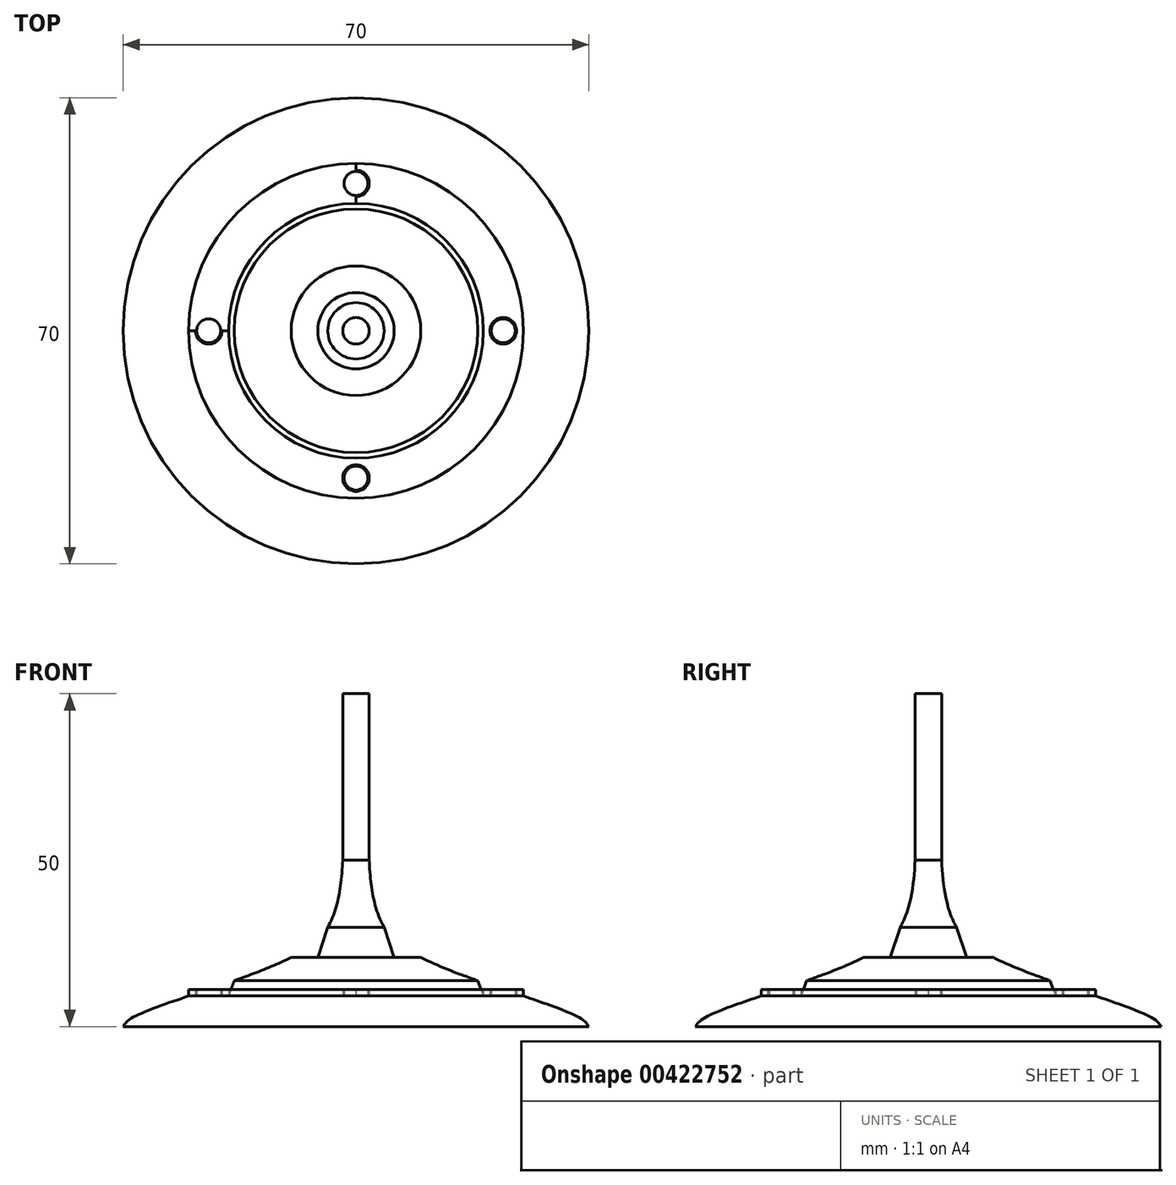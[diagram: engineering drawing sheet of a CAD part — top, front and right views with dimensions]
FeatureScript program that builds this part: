
annotation { "Feature Type Name" : "Feature", "Feature Type Description" : "" }
export const myFeature = defineFeature(function(context is Context, id is Id, definition is map)
    precondition{}
    {
        {
            var Q0;
            Q0=qCreatedBy(makeId("Front.planeOp"),FACE);
            var sketch = newSketch(context, id + "F0", { "sketchPlane" : qUnion([Q0])});
            skLineSegment(sketch, "E0", {"start": v(0, 0) * mm, "end": v(-35, 0) * mm});
            skLineSegment(sketch, "E1", {"start": v(0, 0) * mm, "end": v(0, 50) * mm});
            skLineSegment(sketch, "E2.bottom", {"start": v(0, 50) * mm, "end": v(-2, 50) * mm});
            skLineSegment(sketch, "E2.top", {"start": v(0, 25) * mm, "end": v(-2, 25) * mm});
            skLineSegment(sketch, "E2.left", {"start": v(0, 50) * mm, "end": v(0, 25) * mm});
            skLineSegment(sketch, "E2.right", {"start": v(-2, 50) * mm, "end": v(-2, 25) * mm});
            skLineSegment(sketch, "E3", {"start": v(0, 10.57) * mm, "end": v(-1, 10.57) * mm});
            skPoint(sketch, "E3.endSnap0", {"position": v(-1, 25) * mm});
            skFitSpline(sketch, "E4", {"points": [v(-35, 0) * mm, v(-33.81, 1.19) * mm, v(-25.13, 4.58) * mm, v(-18.3, 6.9) * mm, v(-9.74, 10.37) * mm, v(-4.24, 14.92) * mm, v(-2, 25) * mm], "startDerivative": vector(9.24, 13.84) * mm, "endDerivative": vector(1.73, 56.25) * mm});
            skLineSegment(sketch, "E5", {"start": v(-25.13, 4.58) * mm, "end": v(-19.13, 4.58) * mm});
            skLineSegment(sketch, "E6", {"start": v(-19.13, 4.58) * mm, "end": v(-18.3, 6.9) * mm});
            skLineSegment(sketch, "E7", {"start": v(-9.74, 10.37) * mm, "end": v(-5.74, 10.37) * mm});
            skLineSegment(sketch, "E8", {"start": v(-5.74, 10.37) * mm, "end": v(-4.24, 14.92) * mm});
            skSolve(sketch);
        }
        {
            var Q0;
            Q0=makeQuery(id+"F0.imprint","IMPRINT",FACE,{"disambiguationData":[TD([[makeQuery(id+"F0.imprint","IMPRINT",EDGE,{"derivedFrom":sQuery(id+"F0.wireOp",EDGE,"E2.bottom")}),1.0]])]});
            var Q1;
            {var subQ3=sQuery(id+"F0.wireOp",EDGE,"E0");Q1=makeQuery(id+"F0.imprint","IMPRINT",FACE,{"disambiguationData":[TD([[makeQuery(id+"F0.imprint","IMPRINT",EDGE,{"derivedFrom":subQ3}),-1.0]])]});}
            var Q2;
            Q2=sQuery(id+"F0.wireOp",EDGE,"E1");
            revolve(context, id + "F1", {"entities" : qUnion([Q0, Q1]), "axis" : qUnion([Q2]), "revolveType" : RevolveType.FULL});
        }
        {
            var Q0;
            Q0=makeQuery(id+"F1.opRevolve","SWEPT_FACE",FACE,{"disambiguationData":[OSD([sQuery(id+"F0.wireOp",EDGE,"E5")])]});
            var sketch = newSketch(context, id + "F2", { "sketchPlane" : qUnion([Q0])});
            skLineSegment(sketch, "E9", {"start": v(0, -19.13) * mm, "end": v(0, -25.13) * mm});
            skCircle(sketch, "E10", {"center": v(0, -22.13) * mm, "radius": 2 * mm});
            skCircle(sketch, "E11.0", {"center": v(0, -22.13) * mm, "radius": 1.8 * mm});
            skLineSegment(sketch, "E12", {"start": v(19.13, 0) * mm, "end": v(25.13, 0) * mm});
            skCircle(sketch, "E13", {"center": v(22.13, 0) * mm, "radius": 2 * mm});
            skCircle(sketch, "E14.0", {"center": v(22.13, 0) * mm, "radius": 1.8 * mm});
            skLineSegment(sketch, "E15", {"start": v(0, 19.13) * mm, "end": v(0, 25.13) * mm});
            skCircle(sketch, "E16", {"center": v(0, 22.13) * mm, "radius": 2 * mm});
            skCircle(sketch, "E17.0", {"center": v(0, 22.13) * mm, "radius": 1.8 * mm});
            skLineSegment(sketch, "E18", {"start": v(-19.13, 0) * mm, "end": v(-25.13, 0) * mm});
            skCircle(sketch, "E19", {"center": v(-22.13, 0) * mm, "radius": 2 * mm});
            skCircle(sketch, "E20.0", {"center": v(-22.13, 0) * mm, "radius": 1.8 * mm});
            skSolve(sketch);
        }
        {
            var Q0;
            {var subQ6=sQuery(id+"F2.wireOp",EDGE,"E10");var subQ7=sQuery(id+"F2.wireOp",EDGE,"E9");var subQ8=makeQuery(id+"F2.imprint","INTERSECT",VERTEX,{"disambiguationData":[OD(0.0)],"derivedFrom":[subQ7,subQ6]});Q0=makeQuery(id+"F2.imprint","IMPRINT",FACE,{"disambiguationData":[TD([[makeQuery(id+"F2.imprint","IMPRINT",EDGE,{"disambiguationData":[TD([[subQ8,-1.0]])],"derivedFrom":subQ6}),-1.0]])]});}
            var Q1;
            {var subQ0=sQuery(id+"F2.wireOp",EDGE,"E10");var subQ1=sQuery(id+"F2.wireOp",EDGE,"E9");var subQ2=makeQuery(id+"F2.imprint","INTERSECT",VERTEX,{"disambiguationData":[OD(0.0)],"derivedFrom":[subQ1,subQ0]});Q1=makeQuery(id+"F2.imprint","IMPRINT",FACE,{"disambiguationData":[TD([[makeQuery(id+"F2.imprint","IMPRINT",EDGE,{"disambiguationData":[TD([[subQ2,1.0]])],"derivedFrom":subQ0}),-1.0]])]});}
            var Q2;
            {var subQ6=sQuery(id+"F2.wireOp",EDGE,"E12");var subQ9=sQuery(id+"F2.wireOp",EDGE,"E13");var subQ12=makeQuery(id+"F2.imprint","INTERSECT",VERTEX,{"disambiguationData":[OD(0.0)],"derivedFrom":[subQ6,subQ9]});Q2=makeQuery(id+"F2.imprint","IMPRINT",FACE,{"disambiguationData":[TD([[makeQuery(id+"F2.imprint","IMPRINT",EDGE,{"disambiguationData":[TD([[subQ12,1.0]])],"derivedFrom":subQ9}),-1.0]])]});}
            var Q3;
            {var subQ6=sQuery(id+"F2.wireOp",EDGE,"E15");var subQ9=sQuery(id+"F2.wireOp",EDGE,"E16");var subQ11=makeQuery(id+"F2.imprint","INTERSECT",VERTEX,{"disambiguationData":[OD(0.0)],"derivedFrom":[subQ6,subQ9]});Q3=makeQuery(id+"F2.imprint","IMPRINT",FACE,{"disambiguationData":[TD([[makeQuery(id+"F2.imprint","IMPRINT",EDGE,{"disambiguationData":[TD([[subQ11,1.0]])],"derivedFrom":subQ9}),-1.0]])]});}
            var Q4;
            {var subQ0=sQuery(id+"F2.wireOp",EDGE,"E11.0");var subQ1=sQuery(id+"F2.wireOp",EDGE,"E9");var subQ2=makeQuery(id+"F2.imprint","INTERSECT",VERTEX,{"disambiguationData":[OD(0.0)],"derivedFrom":[subQ1,subQ0]});Q4=makeQuery(id+"F2.imprint","IMPRINT",FACE,{"disambiguationData":[TD([[makeQuery(id+"F2.imprint","IMPRINT",EDGE,{"disambiguationData":[TD([[subQ2,-1.0]])],"derivedFrom":subQ1}),1.0]])]});}
            var Q5;
            {var subQ0=sQuery(id+"F2.wireOp",EDGE,"E11.0");var subQ1=sQuery(id+"F2.wireOp",EDGE,"E9");var subQ2=makeQuery(id+"F2.imprint","INTERSECT",VERTEX,{"disambiguationData":[OD(0.0)],"derivedFrom":[subQ1,subQ0]});Q5=makeQuery(id+"F2.imprint","IMPRINT",FACE,{"disambiguationData":[TD([[makeQuery(id+"F2.imprint","IMPRINT",EDGE,{"disambiguationData":[TD([[subQ2,-1.0]])],"derivedFrom":subQ1}),-1.0]])]});}
            var Q6;
            {var subQ0=sQuery(id+"F2.wireOp",EDGE,"E20.0");var subQ1=sQuery(id+"F2.wireOp",EDGE,"E18");var subQ2=makeQuery(id+"F2.imprint","INTERSECT",VERTEX,{"disambiguationData":[OD(0.0)],"derivedFrom":[subQ1,subQ0]});Q6=makeQuery(id+"F2.imprint","IMPRINT",FACE,{"disambiguationData":[TD([[makeQuery(id+"F2.imprint","IMPRINT",EDGE,{"disambiguationData":[TD([[subQ2,-1.0]])],"derivedFrom":subQ1}),1.0]])]});}
            var Q7;
            {var subQ0=sQuery(id+"F2.wireOp",EDGE,"E20.0");var subQ1=sQuery(id+"F2.wireOp",EDGE,"E18");var subQ2=makeQuery(id+"F2.imprint","INTERSECT",VERTEX,{"disambiguationData":[OD(0.0)],"derivedFrom":[subQ1,subQ0]});Q7=makeQuery(id+"F2.imprint","IMPRINT",FACE,{"disambiguationData":[TD([[makeQuery(id+"F2.imprint","IMPRINT",EDGE,{"disambiguationData":[TD([[subQ2,-1.0]])],"derivedFrom":subQ1}),-1.0]])]});}
            var Q8;
            {var subQ0=sQuery(id+"F2.wireOp",EDGE,"E14.0");var subQ1=sQuery(id+"F2.wireOp",EDGE,"E12");var subQ2=makeQuery(id+"F2.imprint","INTERSECT",VERTEX,{"disambiguationData":[OD(0.0)],"derivedFrom":[subQ1,subQ0]});Q8=makeQuery(id+"F2.imprint","IMPRINT",FACE,{"disambiguationData":[TD([[makeQuery(id+"F2.imprint","IMPRINT",EDGE,{"disambiguationData":[TD([[subQ2,-1.0]])],"derivedFrom":subQ1}),1.0]])]});}
            var Q9;
            {var subQ0=sQuery(id+"F2.wireOp",EDGE,"E14.0");var subQ1=sQuery(id+"F2.wireOp",EDGE,"E12");var subQ2=makeQuery(id+"F2.imprint","INTERSECT",VERTEX,{"disambiguationData":[OD(0.0)],"derivedFrom":[subQ1,subQ0]});Q9=makeQuery(id+"F2.imprint","IMPRINT",FACE,{"disambiguationData":[TD([[makeQuery(id+"F2.imprint","IMPRINT",EDGE,{"disambiguationData":[TD([[subQ2,-1.0]])],"derivedFrom":subQ1}),-1.0]])]});}
            var Q10;
            {var subQ0=sQuery(id+"F2.wireOp",EDGE,"E17.0");var subQ1=sQuery(id+"F2.wireOp",EDGE,"E15");var subQ2=makeQuery(id+"F2.imprint","INTERSECT",VERTEX,{"disambiguationData":[OD(0.0)],"derivedFrom":[subQ1,subQ0]});Q10=makeQuery(id+"F2.imprint","IMPRINT",FACE,{"disambiguationData":[TD([[makeQuery(id+"F2.imprint","IMPRINT",EDGE,{"disambiguationData":[TD([[subQ2,-1.0]])],"derivedFrom":subQ1}),1.0]])]});}
            var Q11;
            {var subQ0=sQuery(id+"F2.wireOp",EDGE,"E17.0");var subQ1=sQuery(id+"F2.wireOp",EDGE,"E15");var subQ2=makeQuery(id+"F2.imprint","INTERSECT",VERTEX,{"disambiguationData":[OD(0.0)],"derivedFrom":[subQ1,subQ0]});Q11=makeQuery(id+"F2.imprint","IMPRINT",FACE,{"disambiguationData":[TD([[makeQuery(id+"F2.imprint","IMPRINT",EDGE,{"disambiguationData":[TD([[subQ2,-1.0]])],"derivedFrom":subQ1}),-1.0]])]});}
            extrude(context, id + "F3", {"entities" : qUnion([Q0, Q1, Q2, Q3, Q4, Q5, Q6, Q7, Q8, Q9, Q10, Q11]), "operationType" : NewBodyOperationType.ADD, "depth" : 1 * mm});
        }
    });
